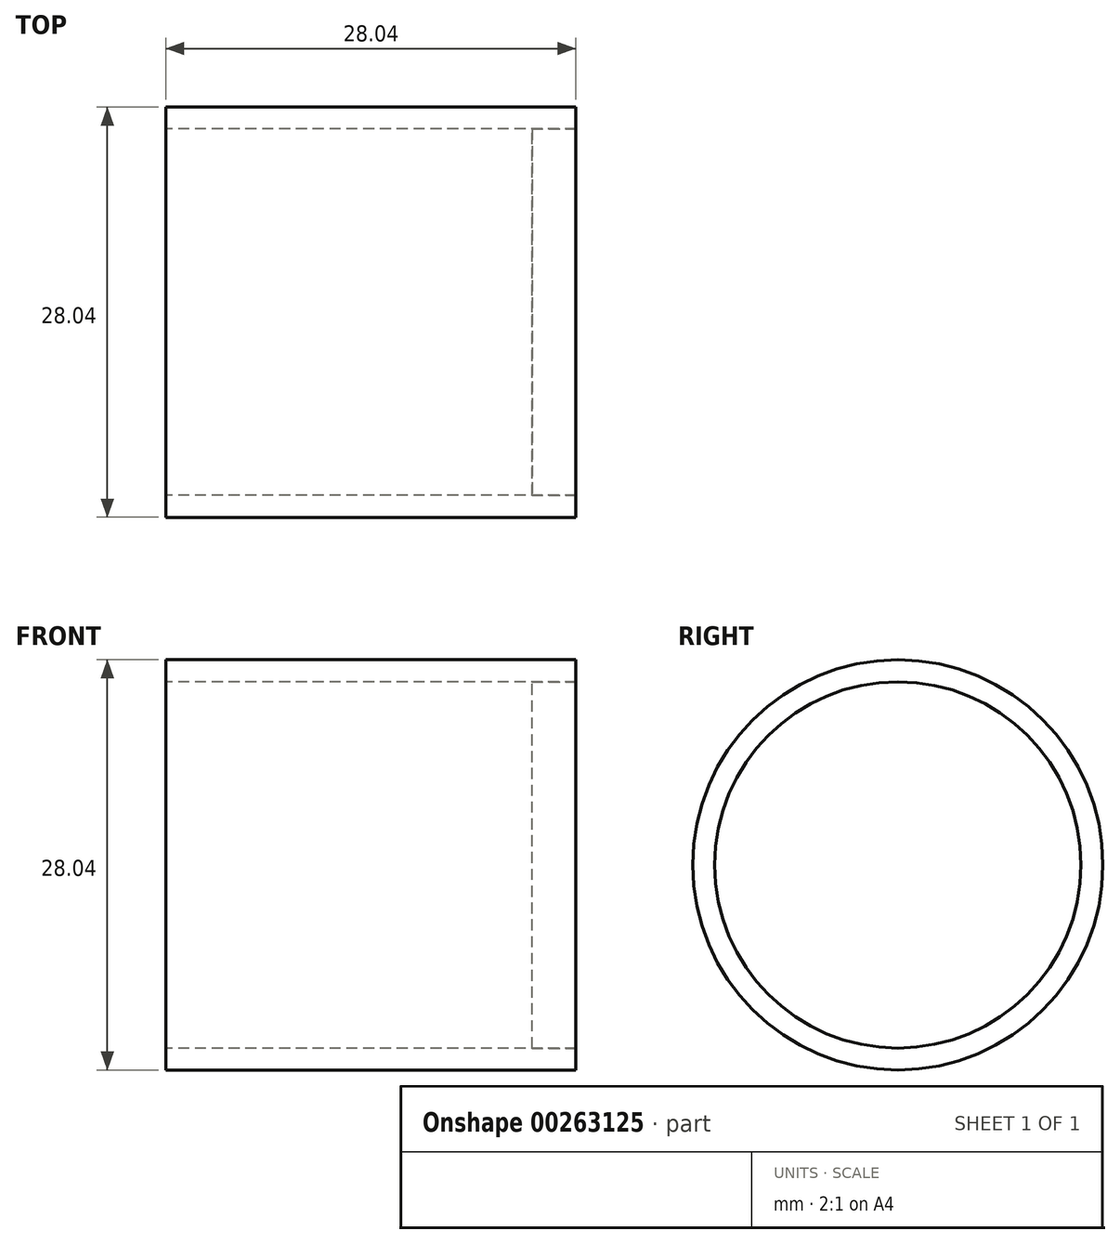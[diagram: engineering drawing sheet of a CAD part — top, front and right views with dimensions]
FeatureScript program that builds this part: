
annotation { "Feature Type Name" : "Feature", "Feature Type Description" : "" }
export const myFeature = defineFeature(function(context is Context, id is Id, definition is map)
    precondition{}
    {
        {
            var Q0;
            Q0=qCreatedBy(makeId("Right.planeOp"),FACE);
            var sketch = newSketch(context, id + "F0", { "sketchPlane" : qUnion([Q0])});
            skCircle(sketch, "E0", {"center": v(0, 0) * mm, "radius": 14.02 * mm});
            skCircle(sketch, "E1", {"center": v(0, 0) * mm, "radius": 12.52 * mm});
            skSolve(sketch);
        }
        {
            var Q0;
            Q0 = qSketchRegion(id + "F0", true);
            extrude(context, id + "F1", {"entities" : qUnion([Q0]), "depth" : 28.04 * mm});
        }
        {
            var Q0;
            Q0=makeQuery(id+"F1.opExtrude","CAP_FACE",FACE,{"disambiguationData":[OSD([sQuery(id+"F0.wireOp",EDGE,"E0"),sQuery(id+"F0.wireOp",EDGE,"E1")])],"isStart":false});
            var sketch = newSketch(context, id + "F2", { "sketchPlane" : qUnion([Q0])});
            skCircle(sketch, "E2", {"center": v(0, 0) * mm, "radius": 13.39 * mm});
            skSolve(sketch);
        }
        {
            var Q0;
            Q0=makeQuery(id+"F2.imprint","IMPRINT",FACE,{"disambiguationData":[TD([[makeQuery(id+"F2.imprint","IMPRINT",EDGE,{"derivedFrom":makeQuery(id+"F1.opExtrude","CAP_EDGE",EDGE,{"disambiguationData":[OSD([sQuery(id+"F0.wireOp",EDGE,"E1")])],"isStart":false})}),1.0]])]});
            var Q1;
            Q1=sQuery(id+"F2.wireOp",EDGE,"E2");
            extrude(context, id + "F3", {"entities" : qUnion([Q0]), "surfaceEntities" : qUnion([Q1]), "oppositeDirection" : true, "depth" : 3 * mm});
        }
    });
